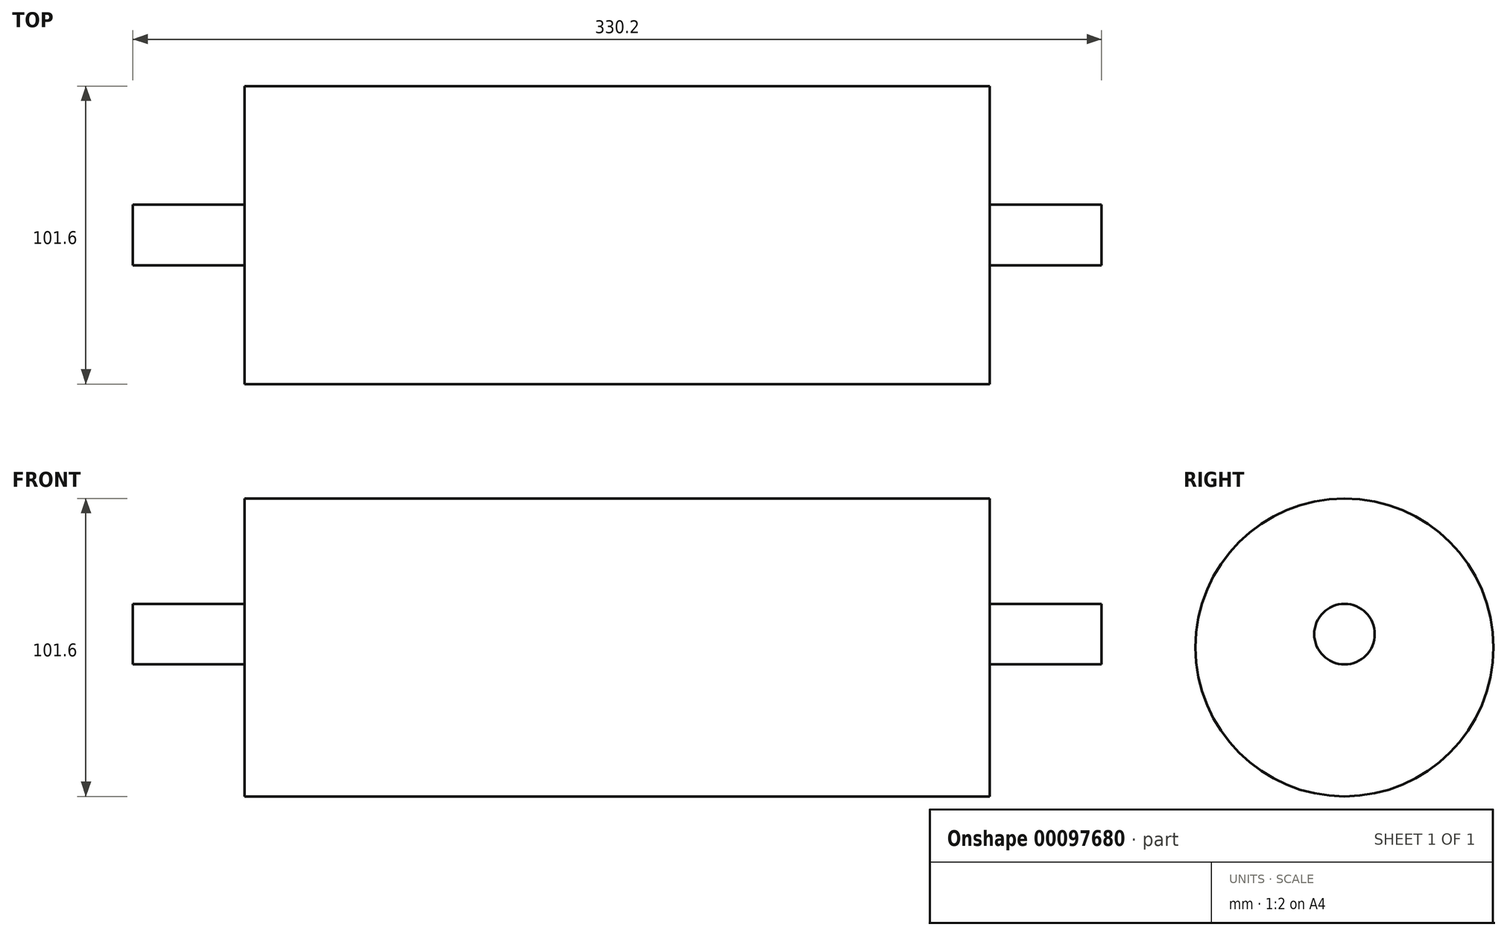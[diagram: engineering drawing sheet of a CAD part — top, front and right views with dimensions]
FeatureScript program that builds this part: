
annotation { "Feature Type Name" : "Feature", "Feature Type Description" : "" }
export const myFeature = defineFeature(function(context is Context, id is Id, definition is map)
    precondition{}
    {
        {
            var Q0;
            Q0=qCreatedBy(makeId("Right.planeOp"),FACE);
            var sketch = newSketch(context, id + "F0", { "sketchPlane" : qUnion([Q0])});
            skCircle(sketch, "E0", {"center": v(0, 0) * mm, "radius": 10.32 * mm});
            skSolve(sketch);
        }
        {
            var Q0;
            Q0 = qSketchRegion(id + "F0", true);
            extrude(context, id + "F1", {"entities" : qUnion([Q0]), "endBound" : BoundingType.SYMMETRIC, "depth" : 330.2 * mm});
        }
        {
            var Q0;
            Q0=qCreatedBy(makeId("Right.planeOp"),FACE);
            var sketch = newSketch(context, id + "F2", { "sketchPlane" : qUnion([Q0])});
            skCircle(sketch, "E1", {"center": v(0, -4.52) * mm, "radius": 50.8 * mm});
            skSolve(sketch);
        }
        {
            var Q0;
            Q0 = qSketchRegion(id + "F2", true);
            extrude(context, id + "F3", {"entities" : qUnion([Q0]), "operationType" : NewBodyOperationType.ADD, "endBound" : BoundingType.SYMMETRIC, "depth" : 254 * mm});
        }
    });
